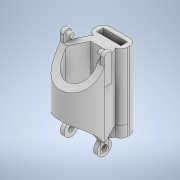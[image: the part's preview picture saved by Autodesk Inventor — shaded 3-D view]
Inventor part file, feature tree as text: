
AUTODESK INVENTOR PART (.ipt)
format: ipt  version: 2022 (Build 260153000, 153)  size: 312,832 bytes
history: native  units: mm
features: extrude x16, sketch x12, other x2, shell x1, fillet x1, projected_geometry x1
ambient origin geometry x8: Origin, YZ Plane, XZ Plane, XY Plane, X Axis, Y Axis, Z Axis, Center Point
bodies: Body1 (feature_tree)
feature tree (33):
  other  "솔리드1"
  sketch  "스케치1"
  extrude  "돌출1"  Depth=20.0mm
  sketch  "스케치7"
  extrude  "돌출7"  Depth=10.0mm
  shell  "쉘2"  Thickness=5.0mm
  extrude  "돌출8"  Depth=30.0mm TaperAngle=0.0deg
  extrude  "돌출9"  Depth=9.0mm
  sketch  "스케치9"
  extrude  "돌출10"  Depth=30.0mm TaperAngle=0.0deg
  sketch  "스케치11"
  sketch  "스케치13"
  sketch  "스케치14"
  extrude  "돌출12"  Depth=3.0mm
  extrude  "돌출13"  Depth=30.0mm TaperAngle=0.0deg
  sketch  "스케치15"
  extrude  "돌출14"  Depth=5.0mm TaperAngle=0.0deg
  extrude  "돌출15"  Depth=5.0mm TaperAngle=0.0deg
  extrude  "돌출16"  Depth=2.0mm
  extrude  "돌출17"  Depth=2.5mm
  other  "작업 평면1"
  extrude  "돌출18"  Depth=8.0mm TaperAngle=0.0deg
  fillet  "모깎기1"  Radius=8.0mm
  extrude  "돌출19"  Depth=100.0mm TaperAngle=0.0deg
  extrude  "돌출20"  Depth=2.0mm TaperAngle=0.0deg
  extrude  "돌출21"  Depth=2.0mm TaperAngle=0.0deg
  extrude  "돌출22"  Depth=5.0mm TaperAngle=0.0deg
  sketch  "스케치8"
  sketch  "스케치10"
  projected_geometry  "투영된 루프1"
  sketch  "스케치16"
  sketch  "스케치17"
  sketch  "스케치18"
